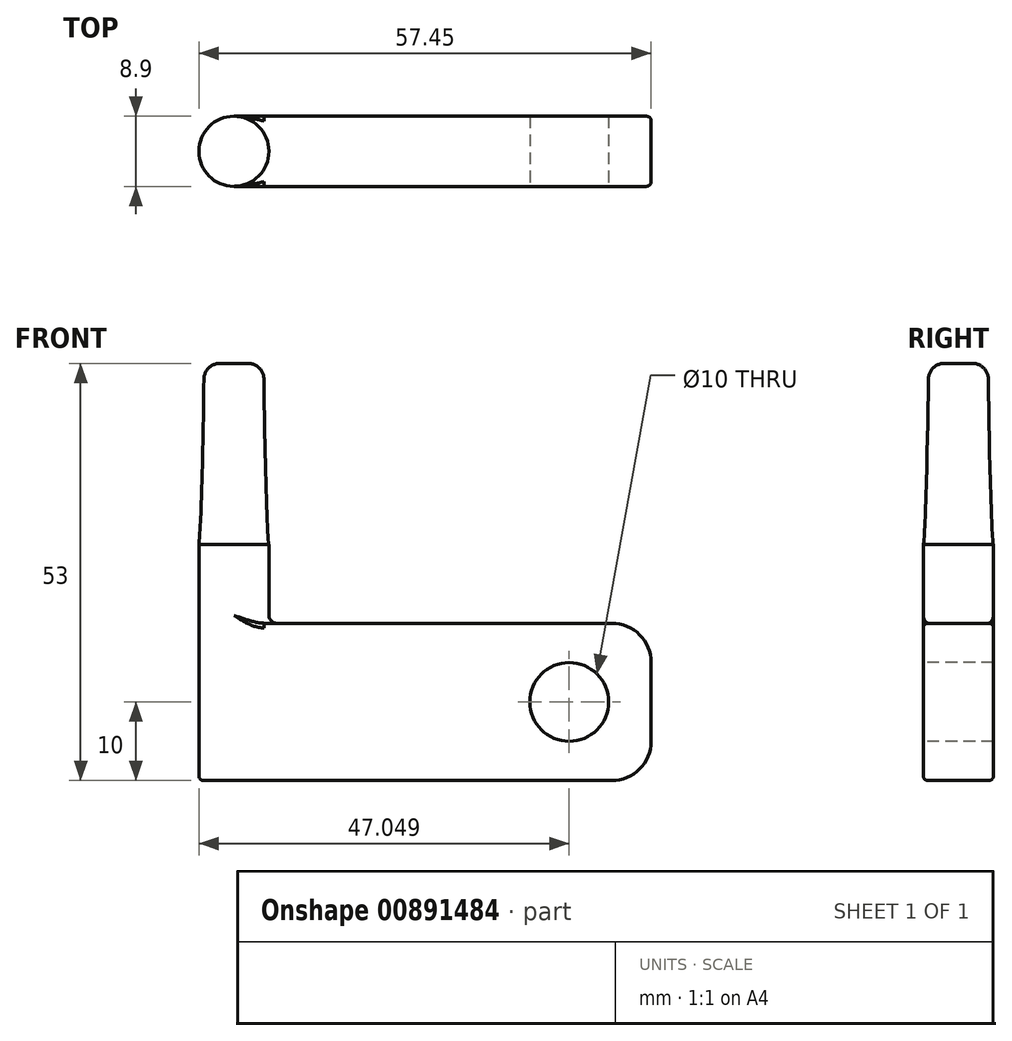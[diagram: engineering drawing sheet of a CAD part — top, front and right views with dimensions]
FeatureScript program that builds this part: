
annotation { "Feature Type Name" : "Feature", "Feature Type Description" : "" }
export const myFeature = defineFeature(function(context is Context, id is Id, definition is map)
    precondition{}
    {
        {
            var Q0;
            Q0=qCreatedBy(makeId("Top.planeOp"),FACE);
            var sketch = newSketch(context, id + "F0", { "sketchPlane" : qUnion([Q0])});
            skCircle(sketch, "E0", {"center": v(0, 0) * mm, "radius": 4.45 * mm});
            skLineSegment(sketch, "E1.bottom", {"start": v(0, 4.45) * mm, "end": v(53, 4.45) * mm});
            skLineSegment(sketch, "E1.top", {"start": v(0, -4.45) * mm, "end": v(53, -4.45) * mm});
            skLineSegment(sketch, "E1.right", {"start": v(53, 4.45) * mm, "end": v(53, -4.45) * mm});
            skSolve(sketch);
        }
        {
            var Q0;
            {var subQ0=sQuery(id+"F0.wireOp",EDGE,"E1.left");var subQ1=sQuery(id+"F0.wireOp",EDGE,"E0");var subQ3=makeQuery(id+"F0.imprint","INTERSECT",VERTEX,{"derivedFrom":[subQ1,subQ0]});Q0=makeQuery(id+"F0.imprint","IMPRINT",FACE,{"disambiguationData":[TD([[makeQuery(id+"F0.imprint","IMPRINT",EDGE,{"disambiguationData":[TD([[subQ3,1.0]])],"derivedFrom":subQ1}),1.0]])]});}
            var Q1;
            {var subQ0=sQuery(id+"F0.wireOp",EDGE,"E1.left");var subQ1=sQuery(id+"F0.wireOp",EDGE,"E0");var subQ3=makeQuery(id+"F0.imprint","INTERSECT",VERTEX,{"derivedFrom":[subQ1,subQ0]});Q1=makeQuery(id+"F0.imprint","IMPRINT",FACE,{"disambiguationData":[TD([[makeQuery(id+"F0.imprint","IMPRINT",EDGE,{"disambiguationData":[TD([[subQ3,-1.0]])],"derivedFrom":subQ1}),1.0]])]});}
            var Q2;
            {var subQ4=sQuery(id+"F0.wireOp",EDGE,"E1.bottom");Q2=makeQuery(id+"F0.imprint","IMPRINT",FACE,{"disambiguationData":[TD([[makeQuery(id+"F0.imprint","IMPRINT",EDGE,{"derivedFrom":subQ4}),-1.0]])]});}
            extrude(context, id + "F1", {"entities" : qUnion([Q0, Q1, Q2]), "depth" : 20 * mm, "offsetDistance" : 25 * mm});
        }
        {
            var Q0;
            {var subQ0=sQuery(id+"F0.wireOp",EDGE,"E0");var subQ1=makeQuery(id+"F0.imprint","INTERSECT",VERTEX,{"derivedFrom":[subQ0,sQuery(id+"F0.wireOp",EDGE,"E1.bottom")]});Q0=makeQuery(id+"F0.imprint","IMPRINT",FACE,{"disambiguationData":[TD([[makeQuery(id+"F0.imprint","IMPRINT",EDGE,{"disambiguationData":[TD([[subQ1,-1.0]])],"derivedFrom":subQ0}),1.0]])]});}
            extrude(context, id + "F2", {"entities" : qUnion([Q0]), "operationType" : NewBodyOperationType.ADD, "depth" : 30 * mm, "offsetDistance" : 25 * mm});
        }
        {
            var Q0;
            Q0=makeQuery(id+"F2.opExtrude","CAP_FACE",FACE,{"disambiguationData":[OSD([sQuery(id+"F0.wireOp",EDGE,"E0")])],"isStart":false});
            var sketch = newSketch(context, id + "F3", { "sketchPlane" : qUnion([Q0])});
            skCircle(sketch, "E2.0", {"center": v(0, 0) * mm, "radius": 4.45 * mm});
            skSolve(sketch);
        }
        {
            var Q0;
            Q0=makeQuery(id+"F3.imprint","IMPRINT",FACE,{"disambiguationData":[TD([[makeQuery(id+"F3.imprint","IMPRINT",EDGE,{"derivedFrom":sQuery(id+"F3.wireOp",EDGE,"E2.0")}),1.0]])]});
            cPlane(context, id + "F4", {"entities" : qUnion([Q0]), "cplaneType" : CPlaneType.OFFSET, "offset" : 23 * mm, "width" : 150 * mm, "height" : 150 * mm});
        }
        {
            var Q0;
            Q0=qCreatedBy(id+"F4.planeOp",FACE);
            var sketch = newSketch(context, id + "F5", { "sketchPlane" : qUnion([Q0])});
            skPoint(sketch, "E3.0", {"position": v(0, 0) * mm});
            skCircle(sketch, "E4", {"center": v(0, 0) * mm, "radius": 3.8 * mm});
            skSolve(sketch);
        }
        {
            var Q0;
            Q0=makeQuery(id+"F3.imprint","IMPRINT",FACE,{"disambiguationData":[TD([[makeQuery(id+"F3.imprint","IMPRINT",EDGE,{"derivedFrom":sQuery(id+"F3.wireOp",EDGE,"E2.0")}),1.0]])]});
            var Q1;
            Q1=makeQuery(id+"F5.imprint","IMPRINT",FACE,{"disambiguationData":[TD([[makeQuery(id+"F5.imprint","IMPRINT",EDGE,{"derivedFrom":sQuery(id+"F5.wireOp",EDGE,"E4")}),1.0]])]});
            loft(context, id + "F6", {"startCondition" : LoftEndDerivativeType.TANGENT_TO_PROFILE, "startMagnitude" : 1, "endCondition" : LoftEndDerivativeType.NORMAL_TO_PROFILE, "endMagnitude" : 1, "sheetProfilesArray" : [{ "sheetProfileEntities" : qUnion([Q0]) }, { "sheetProfileEntities" : qUnion([Q1]) }]});
        }
        {
            var Q0;
            Q0=makeQuery(id+"F6.opLoft","MID_CAP_EDGE",EDGE,{"disambiguationData":[OSD([sQuery(id+"F5.wireOp",EDGE,"E4")])],"capPos":1.0});
            fillet(context, id + "F7", {"entities" : qUnion([Q0]), "radius" : 2 * mm, "allowEdgeOverflow" : false});
        }
        {
            var Q0;
            Q0=makeQuery(id+"F1.opExtrude","CAP_EDGE",EDGE,{"disambiguationData":[OSD([sQuery(id+"F0.wireOp",EDGE,"E1.right")])],"isStart":false});
            var Q1;
            Q1=makeQuery(id+"F1.opExtrude","CAP_EDGE",EDGE,{"disambiguationData":[OSD([sQuery(id+"F0.wireOp",EDGE,"E1.right")])],"isStart":true});
            fillet(context, id + "F8", {"entities" : qUnion([Q0, Q1]), "radius" : 5 * mm, "tangentPropagation" : true, "allowEdgeOverflow" : false});
        }
        {
            var Q0;
            {var subQ0=sQuery(id+"F0.wireOp",EDGE,"E0");Q0=makeQuery(id+"F2.boolean.opBoolean","INTERSECT",EDGE,{"derivedFrom":[makeQuery(id+"F1.opExtrude","CAP_FACE",FACE,{"disambiguationData":[OSD([subQ0,sQuery(id+"F0.wireOp",EDGE,"E1.bottom"),sQuery(id+"F0.wireOp",EDGE,"E1.top"),sQuery(id+"F0.wireOp",EDGE,"E1.right")])],"isStart":false}),makeQuery(id+"F2.opExtrude","SWEPT_FACE",FACE,{"disambiguationData":[OSD([subQ0])]})]});}
            fillet(context, id + "F9", {"entities" : qUnion([Q0]), "radius" : 1 * mm, "tangentPropagation" : true, "allowEdgeOverflow" : false});
        }
        {
            var Q0;
            Q0=makeQuery(id+"F1.opExtrude","SWEPT_FACE",FACE,{"disambiguationData":[OSD([sQuery(id+"F0.wireOp",EDGE,"E1.top")])]});
            var sketch = newSketch(context, id + "F10", { "sketchPlane" : qUnion([Q0])});
            skCircle(sketch, "E5", {"center": v(42.6, 10) * mm, "radius": 5 * mm});
            skPoint(sketch, "E5.centerSnap0", {"position": v(53, 10) * mm});
            skSolve(sketch);
        }
        {
            var Q0;
            Q0=makeQuery(id+"F10.imprint","IMPRINT",FACE,{"disambiguationData":[TD([[makeQuery(id+"F10.imprint","IMPRINT",EDGE,{"derivedFrom":sQuery(id+"F10.wireOp",EDGE,"E5")}),1.0]])]});
            var Q1;
            Q1=makeQuery(id+"F1.opExtrude","SWEPT_FACE",FACE,{"disambiguationData":[OSD([sQuery(id+"F0.wireOp",EDGE,"E1.bottom")])]});
            extrude(context, id + "F11", {"entities" : qUnion([Q0]), "operationType" : NewBodyOperationType.REMOVE, "endBound" : BoundingType.UP_TO_SURFACE, "oppositeDirection" : true, "depth" : 25 * mm, "endBoundEntityFace" : qUnion([Q1]), "offsetDistance" : 25 * mm});
        }
        {
            var Q0;
            Q0=makeQuery(id+"F1.opExtrude","CAP_EDGE",EDGE,{"disambiguationData":[OSD([sQuery(id+"F0.wireOp",EDGE,"E1.top")])],"isStart":false});
            fillet(context, id + "F12", {"entities" : qUnion([Q0]), "radius" : 0.6 * mm, "tangentPropagation" : true, "allowEdgeOverflow" : false});
        }
    });
